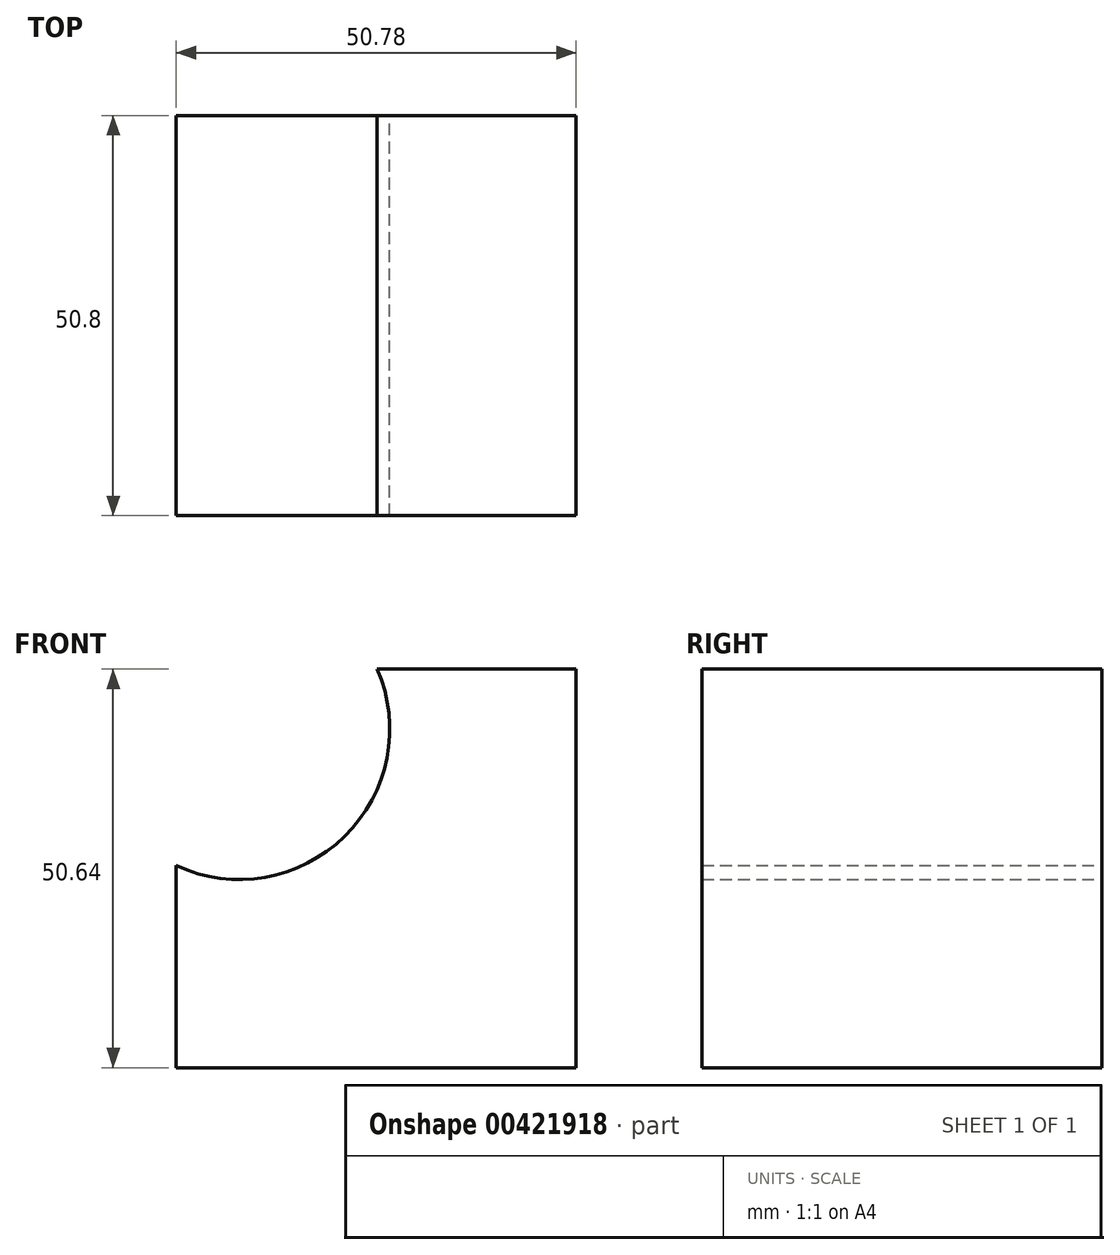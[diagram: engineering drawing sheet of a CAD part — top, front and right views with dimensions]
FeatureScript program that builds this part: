
annotation { "Feature Type Name" : "Feature", "Feature Type Description" : "" }
export const myFeature = defineFeature(function(context is Context, id is Id, definition is map)
    precondition{}
    {
        {
            var Q0;
            Q0=qCreatedBy(makeId("Front.planeOp"),FACE);
            var sketch = newSketch(context, id + "F0", { "sketchPlane" : qUnion([Q0])});
            skLineSegment(sketch, "E0", {"start": v(0, 0) * mm, "end": v(0, 50.64) * mm});
            skLineSegment(sketch, "E1", {"start": v(0, 0) * mm, "end": v(-50.78, 0) * mm});
            skPoint(sketch, "E2.start.orphan", {"position": v(-50.78, 50.64) * mm});
            skLineSegment(sketch, "E3", {"start": v(0, 50.64) * mm, "end": v(-25.25, 50.64) * mm});
            skLineSegment(sketch, "E4", {"start": v(-50.78, 0) * mm, "end": v(-50.78, 25.66) * mm});
            skArc(sketch, "E5", {"start": v(-50.78, 25.66) * mm, "mid": v(-29.42, 29.36) * mm, "end": v(-25.25, 50.64) * mm});
            skSolve(sketch);
        }
        {
            var Q0;
            Q0 = qSketchRegion(id + "F0", true);
            extrude(context, id + "F1", {"entities" : qUnion([Q0]), "depth" : 50.8 * mm});
        }
    });
